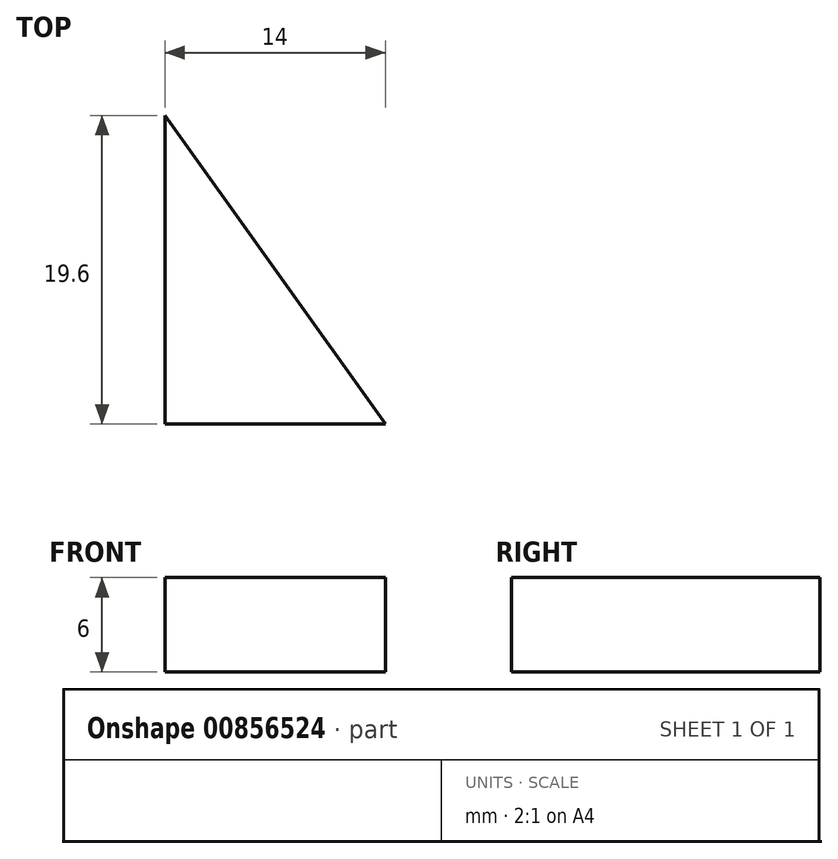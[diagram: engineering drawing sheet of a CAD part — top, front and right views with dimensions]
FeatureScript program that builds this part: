
annotation { "Feature Type Name" : "Feature", "Feature Type Description" : "" }
export const myFeature = defineFeature(function(context is Context, id is Id, definition is map)
    precondition{}
    {
        {
            var Q0;
            Q0=qCreatedBy(makeId("Front.planeOp"),FACE);
            var sketch = newSketch(context, id + "F0", { "sketchPlane" : qUnion([Q0])});
            skLineSegment(sketch, "E0.bottom", {"start": v(7, 3) * mm, "end": v(-7, 3) * mm});
            skLineSegment(sketch, "E0.top", {"start": v(7, -3) * mm, "end": v(-7, -3) * mm});
            skLineSegment(sketch, "E0.left", {"start": v(7, 3) * mm, "end": v(7, -3) * mm});
            skLineSegment(sketch, "E0.right", {"start": v(-7, 3) * mm, "end": v(-7, -3) * mm});
            skPoint(sketch, "E0.middle", {"position": v(0, 0) * mm});
            skSolve(sketch);
        }
        {
            var Q0;
            Q0=makeQuery(id+"F0.imprint","IMPRINT",FACE,{"disambiguationData":[TD([[makeQuery(id+"F0.imprint","IMPRINT",EDGE,{"derivedFrom":sQuery(id+"F0.wireOp",EDGE,"E0.bottom")}),1.0]])]});
            extrude(context, id + "F1", {"entities" : qUnion([Q0]), "depth" : 20 * mm, "offsetDistance" : 25 * mm});
        }
        {
            var Q0;
            Q0=makeQuery(id+"F1.opExtrude","CAP_EDGE",EDGE,{"disambiguationData":[OSD([sQuery(id+"F0.wireOp",EDGE,"E0.left")])],"isStart":true});
            chamfer(context, id + "F2", {"entities" : qUnion([Q0]), "chamferType" : ChamferType.TWO_OFFSETS, "width1" : 14.28 * mm, "oppositeDirection" : false, "width2" : 20 * mm, "tangentPropagation" : true});
        }
    });
